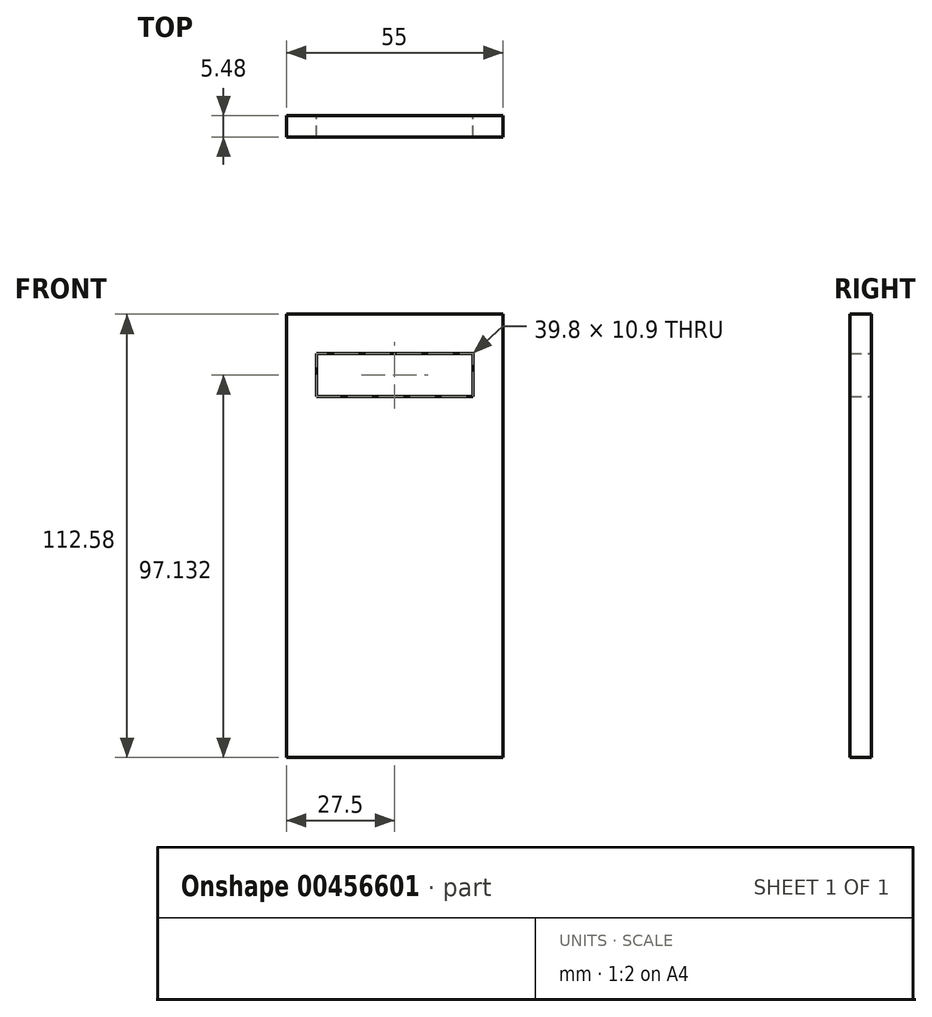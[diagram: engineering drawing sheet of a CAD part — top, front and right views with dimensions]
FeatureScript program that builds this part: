
annotation { "Feature Type Name" : "Feature", "Feature Type Description" : "" }
export const myFeature = defineFeature(function(context is Context, id is Id, definition is map)
    precondition{}
    {
        {
            var Q0;
            Q0=qCreatedBy(makeId("Front.planeOp"),FACE);
            var sketch = newSketch(context, id + "F0", { "sketchPlane" : qUnion([Q0])});
            skLineSegment(sketch, "E0.bottom", {"start": v(27.5, 56.3) * mm, "end": v(-27.5, 56.3) * mm});
            skLineSegment(sketch, "E0.top", {"start": v(27.5, -56.3) * mm, "end": v(-27.5, -56.3) * mm});
            skLineSegment(sketch, "E0.left", {"start": v(27.5, 56.3) * mm, "end": v(27.5, -56.3) * mm});
            skLineSegment(sketch, "E0.right", {"start": v(-27.5, 56.3) * mm, "end": v(-27.5, -56.3) * mm});
            skPoint(sketch, "E0.middle", {"position": v(0, 0) * mm});
            skLineSegment(sketch, "E1.bottom", {"start": v(19.9, 35.4) * mm, "end": v(-19.9, 35.4) * mm});
            skLineSegment(sketch, "E1.top", {"start": v(19.9, 46.3) * mm, "end": v(-19.9, 46.3) * mm});
            skLineSegment(sketch, "E1.left", {"start": v(19.9, 35.4) * mm, "end": v(19.9, 46.3) * mm});
            skLineSegment(sketch, "E1.right", {"start": v(-19.9, 35.4) * mm, "end": v(-19.9, 46.3) * mm});
            skPoint(sketch, "E1.middle", {"position": v(0, 40.84) * mm});
            skSolve(sketch);
        }
        {
            var Q0;
            Q0=makeQuery(id+"F0.imprint","IMPRINT",FACE,{"disambiguationData":[TD([[makeQuery(id+"F0.imprint","IMPRINT",EDGE,{"derivedFrom":sQuery(id+"F0.wireOp",EDGE,"E0.bottom")}),1.0]])]});
            extrude(context, id + "F1", {"entities" : qUnion([Q0]), "depth" : 5.48 * mm});
        }
    });
